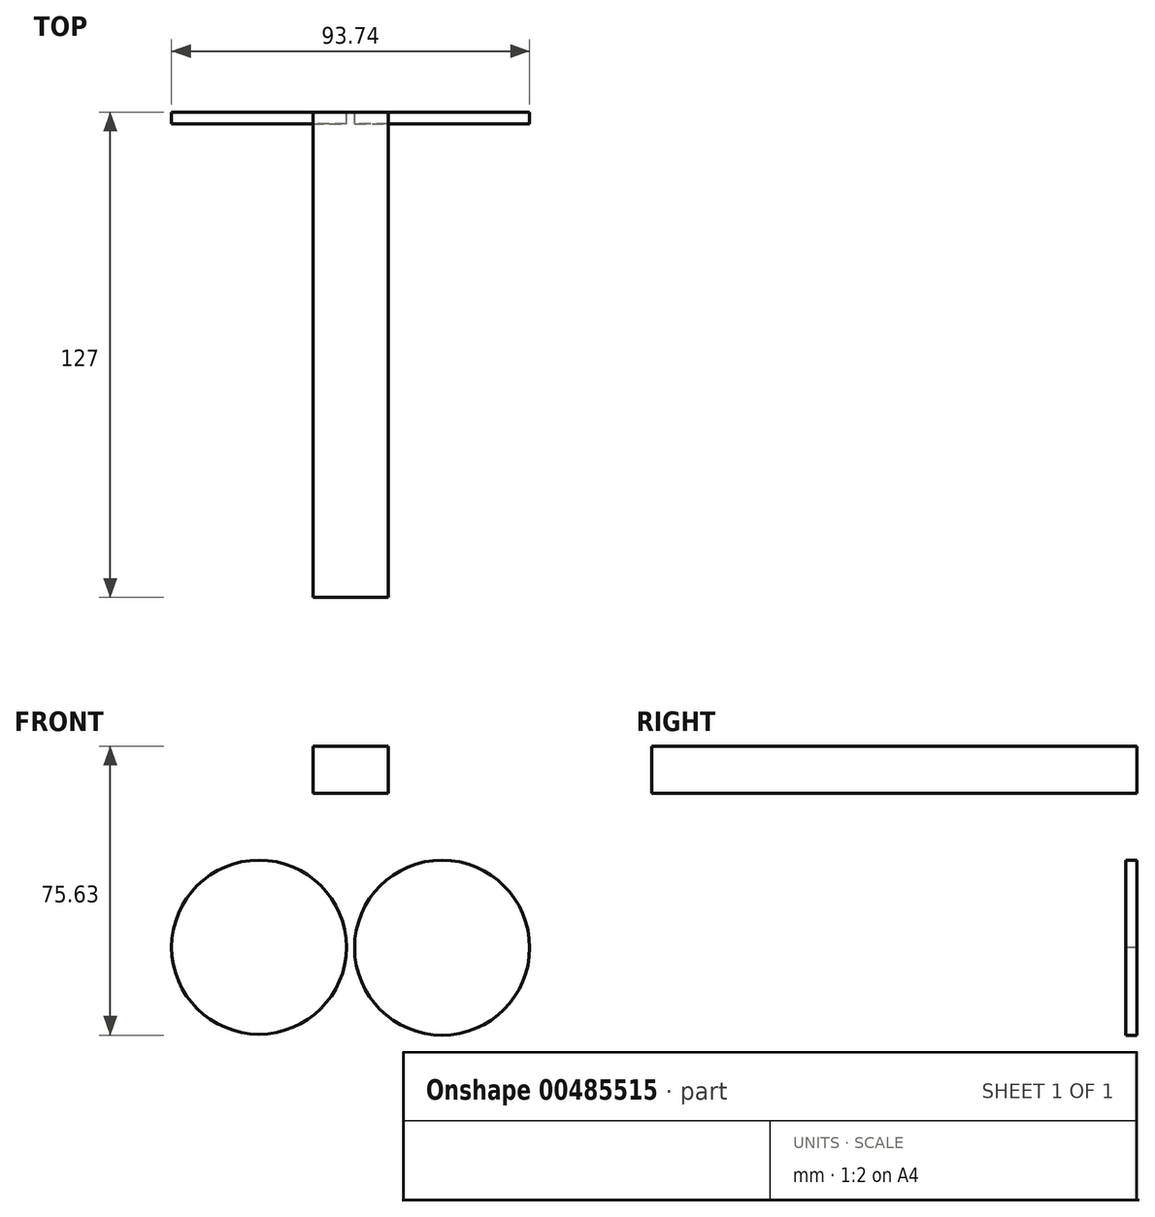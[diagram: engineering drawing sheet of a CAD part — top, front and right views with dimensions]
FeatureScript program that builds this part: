
annotation { "Feature Type Name" : "Feature", "Feature Type Description" : "" }
export const myFeature = defineFeature(function(context is Context, id is Id, definition is map)
    precondition{}
    {
        {
            var Q0;
            Q0=qCreatedBy(makeId("Front.planeOp"),FACE);
            var sketch = newSketch(context, id + "F0", { "sketchPlane" : qUnion([Q0])});
            skCircle(sketch, "E0", {"center": v(-23.96, 0.13) * mm, "radius": 22.9 * mm});
            skCircle(sketch, "E1.MirrorC", {"center": v(-23.96, -0.13) * mm, "radius": 22.9 * mm});
            skCircle(sketch, "E2.MirrorC", {"center": v(23.96, -0.13) * mm, "radius": 22.9 * mm});
            skSolve(sketch);
        }
        {
            var Q0;
            {var subQ0=sQuery(id+"F0.wireOp",EDGE,"E1.MirrorC");var subQ1=sQuery(id+"F0.wireOp",EDGE,"E0");var subQ2=makeQuery(id+"F0.imprint","INTERSECT",VERTEX,{"disambiguationData":[OD(0.0)],"derivedFrom":[subQ1,subQ0]});Q0=makeQuery(id+"F0.imprint","IMPRINT",FACE,{"disambiguationData":[TD([[makeQuery(id+"F0.imprint","IMPRINT",EDGE,{"disambiguationData":[TD([[subQ2,-1.0]])],"derivedFrom":subQ1}),1.0]])]});}
            var Q1;
            Q1=makeQuery(id+"F0.imprint","IMPRINT",FACE,{"disambiguationData":[TD([[makeQuery(id+"F0.imprint","IMPRINT",EDGE,{"derivedFrom":sQuery(id+"F0.wireOp",EDGE,"E2.MirrorC")}),1.0]])]});
            extrude(context, id + "F1", {"entities" : qUnion([Q0, Q1]), "depth" : 3 * mm});
        }
        {
            var Q0;
            Q0=qCreatedBy(makeId("Front.planeOp"),FACE);
            var sketch = newSketch(context, id + "F2", { "sketchPlane" : qUnion([Q0])});
            skLineSegment(sketch, "E3.bottom", {"start": v(-9.85, 52.59) * mm, "end": v(9.85, 52.59) * mm});
            skLineSegment(sketch, "E3.top", {"start": v(-9.85, 40.34) * mm, "end": v(9.85, 40.34) * mm});
            skLineSegment(sketch, "E3.left", {"start": v(-9.85, 52.59) * mm, "end": v(-9.85, 40.34) * mm});
            skLineSegment(sketch, "E3.right", {"start": v(9.85, 52.59) * mm, "end": v(9.85, 40.34) * mm});
            skPoint(sketch, "E3.middle", {"position": v(0, 46.46) * mm});
            skSolve(sketch);
        }
        {
            var Q0;
            Q0=makeQuery(id+"F2.imprint","IMPRINT",FACE,{"disambiguationData":[TD([[makeQuery(id+"F2.imprint","IMPRINT",EDGE,{"derivedFrom":sQuery(id+"F2.wireOp",EDGE,"E3.bottom")}),-1.0]])]});
            extrude(context, id + "F3", {"entities" : qUnion([Q0]), "depth" : 127 * mm});
        }
    });
